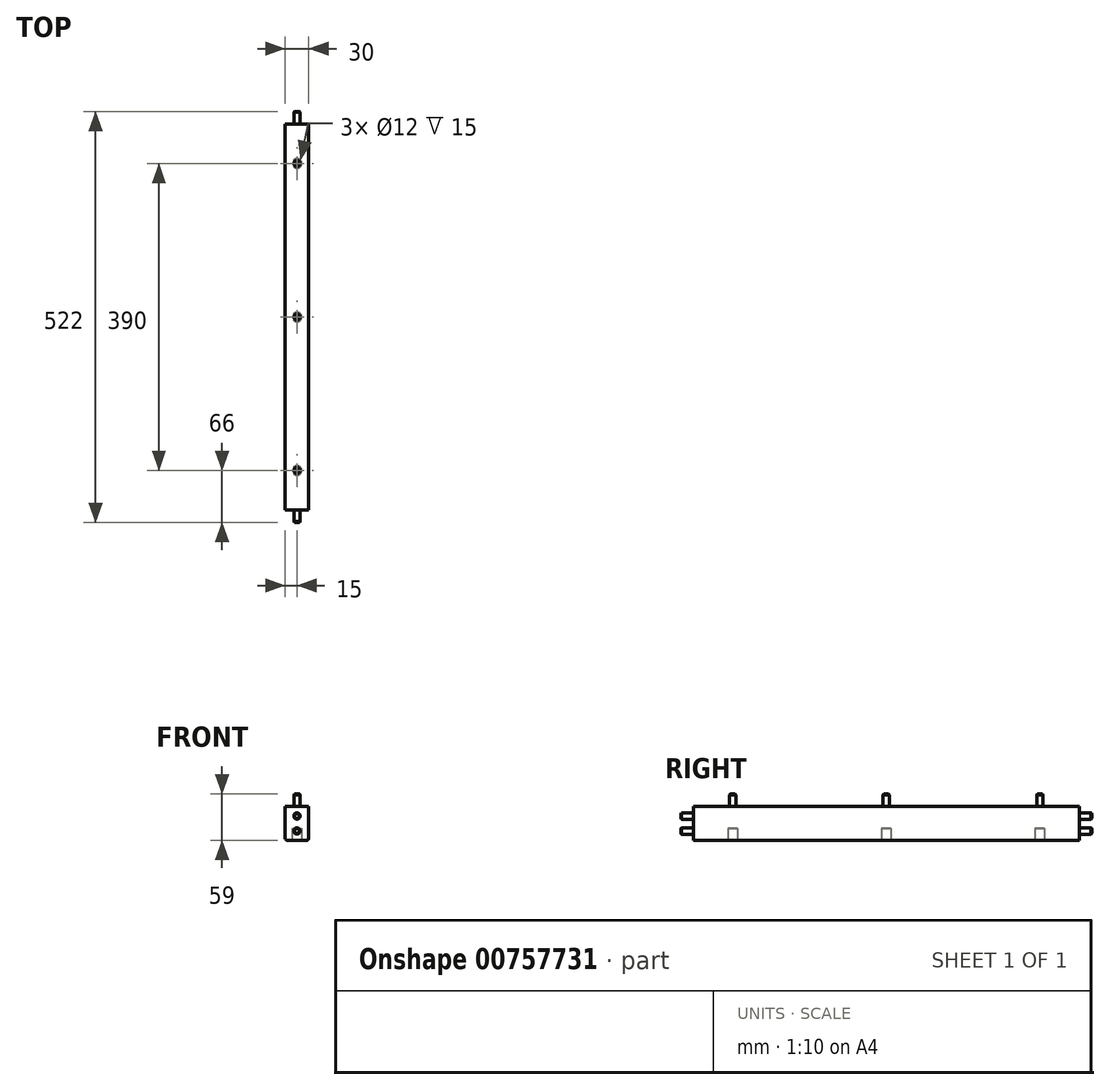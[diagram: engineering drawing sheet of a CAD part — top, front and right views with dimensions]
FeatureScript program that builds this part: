
annotation { "Feature Type Name" : "Feature", "Feature Type Description" : "" }
export const myFeature = defineFeature(function(context is Context, id is Id, definition is map)
    precondition{}
    {
        {
            var Q0;
            Q0=qCreatedBy(makeId("Right.planeOp"),FACE);
            var sketch = newSketch(context, id + "F0", { "sketchPlane" : qUnion([Q0])});
            skLineSegment(sketch, "E0.bottom", {"start": v(245, 21.5) * mm, "end": v(-245, 21.5) * mm});
            skLineSegment(sketch, "E0.top", {"start": v(245, -21.5) * mm, "end": v(-245, -21.5) * mm});
            skLineSegment(sketch, "E0.left", {"start": v(245, 21.5) * mm, "end": v(245, -21.5) * mm});
            skLineSegment(sketch, "E0.right", {"start": v(-245, 21.5) * mm, "end": v(-245, -21.5) * mm});
            skPoint(sketch, "E0.middle", {"position": v(0, 0) * mm});
            skSolve(sketch);
        }
        {
            var Q0;
            Q0=makeQuery(id+"F0.imprint","IMPRINT",FACE,{"disambiguationData":[TD([[makeQuery(id+"F0.imprint","IMPRINT",EDGE,{"derivedFrom":sQuery(id+"F0.wireOp",EDGE,"E0.bottom")}),1.0]])]});
            extrude(context, id + "F1", {"entities" : qUnion([Q0]), "oppositeDirection" : true, "depth" : 30 * mm, "offsetDistance" : 25 * mm});
        }
        {
            var Q0;
            Q0=makeQuery(id+"F1.opExtrude","SWEPT_FACE",FACE,{"disambiguationData":[OSD([sQuery(id+"F0.wireOp",EDGE,"E0.left")])]});
            var sketch = newSketch(context, id + "F2", { "sketchPlane" : qUnion([Q0])});
            skLineSegment(sketch, "E1", {"start": v(15, 21.5) * mm, "end": v(15, -21.5) * mm, "construction": true});
            skCircle(sketch, "E2", {"center": v(15, 9.5) * mm, "radius": 4 * mm});
            skCircle(sketch, "E3", {"center": v(15, -9.5) * mm, "radius": 4 * mm});
            skSolve(sketch);
        }
        {
            var Q0;
            Q0=makeQuery(id+"F2.imprint","IMPRINT",FACE,{"disambiguationData":[TD([[makeQuery(id+"F2.imprint","IMPRINT",EDGE,{"derivedFrom":sQuery(id+"F2.wireOp",EDGE,"E2")}),1.0]])]});
            var Q1;
            Q1=makeQuery(id+"F2.imprint","IMPRINT",FACE,{"disambiguationData":[TD([[makeQuery(id+"F2.imprint","IMPRINT",EDGE,{"derivedFrom":sQuery(id+"F2.wireOp",EDGE,"E3")}),1.0]])]});
            extrude(context, id + "F3", {"entities" : qUnion([Q0, Q1]), "operationType" : NewBodyOperationType.ADD, "depth" : 16 * mm, "offsetDistance" : 25 * mm});
        }
        {
            var Q0;
            Q0=makeQuery(id+"F3.opExtrude","CAP_EDGE",EDGE,{"disambiguationData":[OSD([sQuery(id+"F2.wireOp",EDGE,"E2")])],"isStart":false});
            var Q1;
            Q1=makeQuery(id+"F3.opExtrude","CAP_EDGE",EDGE,{"disambiguationData":[OSD([sQuery(id+"F2.wireOp",EDGE,"E3")])],"isStart":false});
            chamfer(context, id + "F4", {"entities" : qUnion([Q0, Q1]), "width" : 1 * mm, "tangentPropagation" : true});
        }
        {
            var Q0;
            Q0=makeQuery(id+"F1.opExtrude","SWEPT_FACE",FACE,{"disambiguationData":[OSD([sQuery(id+"F0.wireOp",EDGE,"E0.right")])]});
            var sketch = newSketch(context, id + "F5", { "sketchPlane" : qUnion([Q0])});
            skLineSegment(sketch, "E4", {"start": v(-15, 21.5) * mm, "end": v(-15, -21.5) * mm, "construction": true});
            skCircle(sketch, "E5", {"center": v(-15, 9.5) * mm, "radius": 4 * mm});
            skCircle(sketch, "E6", {"center": v(-15, -9.5) * mm, "radius": 4 * mm});
            skSolve(sketch);
        }
        {
            var Q0;
            Q0=makeQuery(id+"F5.imprint","IMPRINT",FACE,{"disambiguationData":[TD([[makeQuery(id+"F5.imprint","IMPRINT",EDGE,{"derivedFrom":sQuery(id+"F5.wireOp",EDGE,"E5")}),1.0]])]});
            var Q1;
            Q1=makeQuery(id+"F5.imprint","IMPRINT",FACE,{"disambiguationData":[TD([[makeQuery(id+"F5.imprint","IMPRINT",EDGE,{"derivedFrom":sQuery(id+"F5.wireOp",EDGE,"E6")}),1.0]])]});
            extrude(context, id + "F6", {"entities" : qUnion([Q0, Q1]), "operationType" : NewBodyOperationType.ADD, "depth" : 16 * mm, "offsetDistance" : 25 * mm});
        }
        {
            var Q0;
            Q0=makeQuery(id+"F6.opExtrude","CAP_EDGE",EDGE,{"disambiguationData":[OSD([sQuery(id+"F5.wireOp",EDGE,"E5")])],"isStart":false});
            var Q1;
            Q1=makeQuery(id+"F6.opExtrude","CAP_EDGE",EDGE,{"disambiguationData":[OSD([sQuery(id+"F5.wireOp",EDGE,"E6")])],"isStart":false});
            chamfer(context, id + "F7", {"entities" : qUnion([Q0, Q1]), "width" : 1 * mm, "tangentPropagation" : true});
        }
        {
            var Q0;
            Q0=makeQuery(id+"F1.opExtrude","CAP_EDGE",EDGE,{"disambiguationData":[OSD([sQuery(id+"F0.wireOp",EDGE,"E0.top")])],"isStart":false});
            var Q1;
            Q1=makeQuery(id+"F1.opExtrude","CAP_EDGE",EDGE,{"disambiguationData":[OSD([sQuery(id+"F0.wireOp",EDGE,"E0.top")])],"isStart":true});
            fillet(context, id + "F8", {"entities" : qUnion([Q0, Q1]), "radius" : 3 * mm, "tangentPropagation" : true, "allowEdgeOverflow" : false});
        }
        {
            var Q0;
            Q0=makeQuery(id+"F1.opExtrude","SWEPT_FACE",FACE,{"disambiguationData":[OSD([sQuery(id+"F0.wireOp",EDGE,"E0.top")])]});
            var sketch = newSketch(context, id + "F9", { "sketchPlane" : qUnion([Q0])});
            skLineSegment(sketch, "E7", {"start": v(-15, 245) * mm, "end": v(-15, -245) * mm, "construction": true});
            skCircle(sketch, "E8", {"center": v(-15, 0) * mm, "radius": 6 * mm});
            skCircle(sketch, "E9", {"center": v(-15, 195) * mm, "radius": 6 * mm});
            skCircle(sketch, "E10", {"center": v(-15, -195) * mm, "radius": 6 * mm});
            skSolve(sketch);
        }
        {
            var Q0;
            Q0=makeQuery(id+"F9.imprint","IMPRINT",FACE,{"disambiguationData":[TD([[makeQuery(id+"F9.imprint","IMPRINT",EDGE,{"derivedFrom":sQuery(id+"F9.wireOp",EDGE,"E9")}),1.0]])]});
            var Q1;
            Q1=makeQuery(id+"F9.imprint","IMPRINT",FACE,{"disambiguationData":[TD([[makeQuery(id+"F9.imprint","IMPRINT",EDGE,{"derivedFrom":sQuery(id+"F9.wireOp",EDGE,"E8")}),1.0]])]});
            var Q2;
            Q2=makeQuery(id+"F9.imprint","IMPRINT",FACE,{"disambiguationData":[TD([[makeQuery(id+"F9.imprint","IMPRINT",EDGE,{"derivedFrom":sQuery(id+"F9.wireOp",EDGE,"E10")}),1.0]])]});
            extrude(context, id + "F10", {"entities" : qUnion([Q0, Q1, Q2]), "operationType" : NewBodyOperationType.REMOVE, "oppositeDirection" : true, "depth" : 15 * mm, "offsetDistance" : 25 * mm});
        }
        {
            var Q0;
            Q0=makeQuery(id+"F1.opExtrude","SWEPT_FACE",FACE,{"disambiguationData":[OSD([sQuery(id+"F0.wireOp",EDGE,"E0.bottom")])]});
            var sketch = newSketch(context, id + "F11", { "sketchPlane" : qUnion([Q0])});
            skLineSegment(sketch, "E11", {"start": v(-15, 245) * mm, "end": v(-15, -245) * mm, "construction": true});
            skCircle(sketch, "E12", {"center": v(-15, 0) * mm, "radius": 4 * mm});
            skCircle(sketch, "E13", {"center": v(-15, 195) * mm, "radius": 4 * mm});
            skCircle(sketch, "E14", {"center": v(-15, -195) * mm, "radius": 4 * mm});
            skSolve(sketch);
        }
        {
            var Q0;
            Q0=makeQuery(id+"F11.imprint","IMPRINT",FACE,{"disambiguationData":[TD([[makeQuery(id+"F11.imprint","IMPRINT",EDGE,{"derivedFrom":sQuery(id+"F11.wireOp",EDGE,"E13")}),1.0]])]});
            var Q1;
            Q1=makeQuery(id+"F11.imprint","IMPRINT",FACE,{"disambiguationData":[TD([[makeQuery(id+"F11.imprint","IMPRINT",EDGE,{"derivedFrom":sQuery(id+"F11.wireOp",EDGE,"E12")}),1.0]])]});
            var Q2;
            Q2=makeQuery(id+"F11.imprint","IMPRINT",FACE,{"disambiguationData":[TD([[makeQuery(id+"F11.imprint","IMPRINT",EDGE,{"derivedFrom":sQuery(id+"F11.wireOp",EDGE,"E14")}),1.0]])]});
            extrude(context, id + "F12", {"entities" : qUnion([Q0, Q1, Q2]), "operationType" : NewBodyOperationType.ADD, "depth" : 16 * mm, "offsetDistance" : 25 * mm});
        }
        {
            var Q0;
            Q0=makeQuery(id+"F12.opExtrude","CAP_EDGE",EDGE,{"disambiguationData":[OSD([sQuery(id+"F11.wireOp",EDGE,"E13")])],"isStart":false});
            var Q1;
            Q1=makeQuery(id+"F12.opExtrude","CAP_EDGE",EDGE,{"disambiguationData":[OSD([sQuery(id+"F11.wireOp",EDGE,"E12")])],"isStart":false});
            var Q2;
            Q2=makeQuery(id+"F12.opExtrude","CAP_EDGE",EDGE,{"disambiguationData":[OSD([sQuery(id+"F11.wireOp",EDGE,"E14")])],"isStart":false});
            chamfer(context, id + "F13", {"entities" : qUnion([Q0, Q1, Q2]), "width" : 1 * mm, "tangentPropagation" : true});
        }
    });
